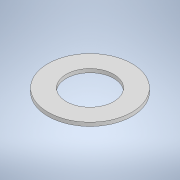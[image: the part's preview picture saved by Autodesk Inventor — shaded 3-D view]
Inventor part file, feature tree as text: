
AUTODESK INVENTOR PART (.ipt)
format: ipt  version: 2020 (Build 240168000, 168)  size: 103,936 bytes
history: native  units: mm
features: revolve x1, sketch x1
ambient origin geometry x8: Origin, YZ Plane, XZ Plane, XY Plane, X Axis, Y Axis, Z Axis, Center Point
bodies: Solid1 (feature_tree)
feature tree (2):
  revolve  "Revolution1"  [1 undecoded]
  sketch  "Sketch2"  dims[d4=90.0deg]
note: 1 required parameter value undecoded (feature->parameter linkage not recoverable at this tier; creation-order binding heuristic only, values carry confidence <= 0.55)
